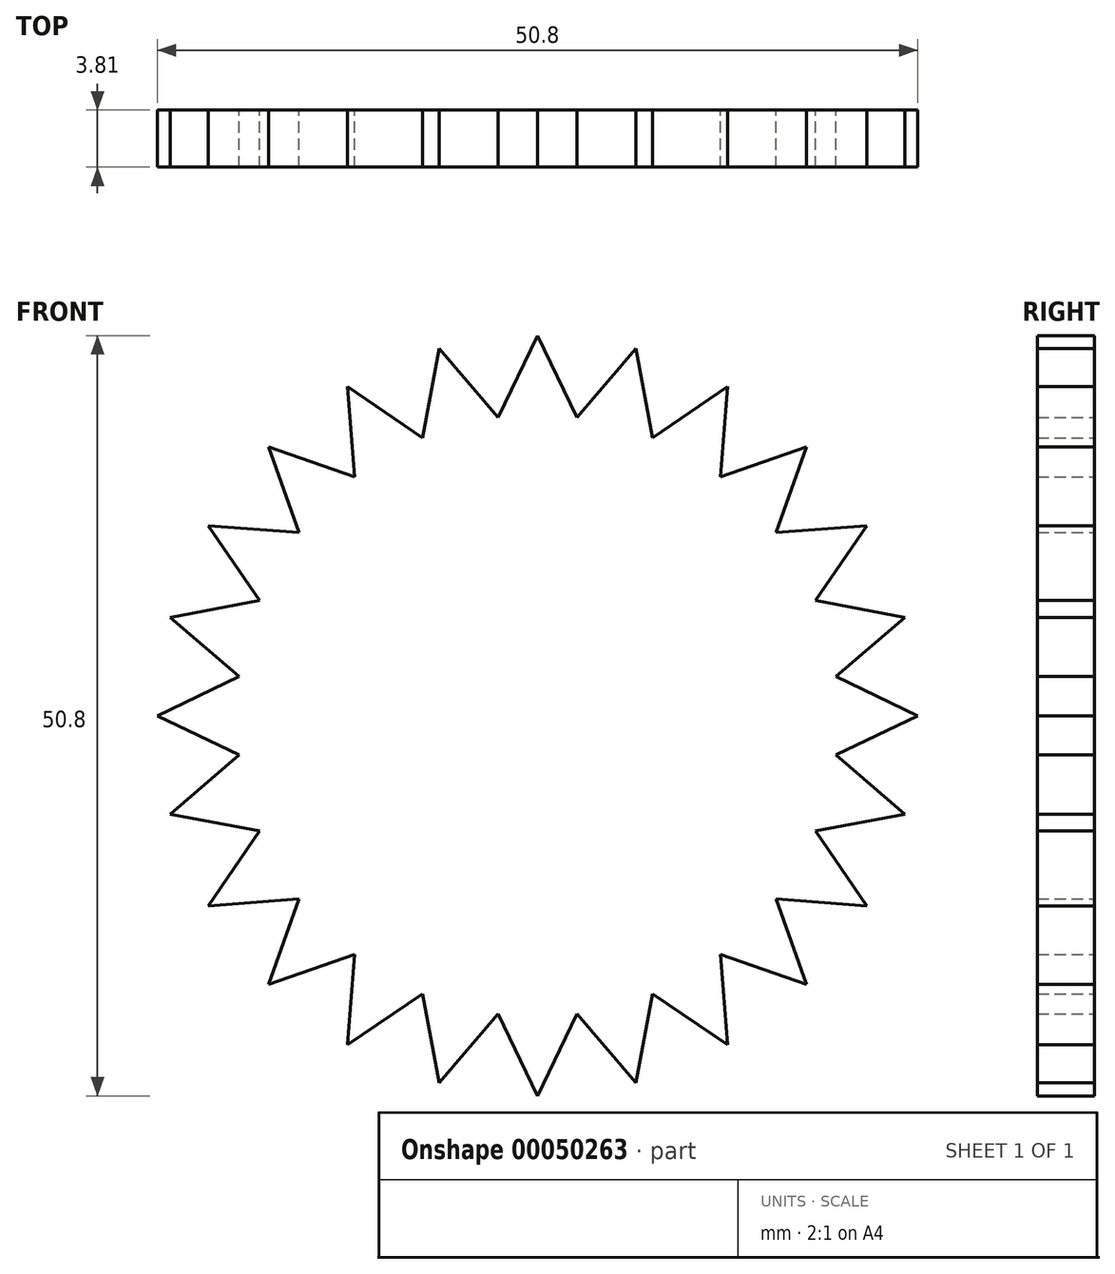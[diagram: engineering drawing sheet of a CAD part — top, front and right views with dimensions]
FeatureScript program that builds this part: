
annotation { "Feature Type Name" : "Feature", "Feature Type Description" : "" }
export const myFeature = defineFeature(function(context is Context, id is Id, definition is map)
    precondition{}
    {
        {
            var Q0;
            Q0=qCreatedBy(makeId("Front.planeOp"),FACE);
            var sketch = newSketch(context, id + "F0", { "sketchPlane" : qUnion([Q0])});
            skLineSegment(sketch, "E0", {"start": v(0, 0) * mm, "end": v(25.4, 0) * mm});
            skLineSegment(sketch, "E1", {"start": v(0, 0) * mm, "end": v(0, 25.4) * mm});
            skLineSegment(sketch, "E2", {"start": v(0, 0) * mm, "end": v(-25.4, 0) * mm});
            skLineSegment(sketch, "E3", {"start": v(0, 0) * mm, "end": v(0, -25.4) * mm});
            skLineSegment(sketch, "E4", {"start": v(0, 0) * mm, "end": v(24.53, -6.57) * mm});
            skLineSegment(sketch, "E5", {"start": v(0, 0) * mm, "end": v(24.53, 6.57) * mm});
            skLineSegment(sketch, "E6", {"start": v(0, 0) * mm, "end": v(22, 12.7) * mm});
            skLineSegment(sketch, "E7", {"start": v(0, 0) * mm, "end": v(17.96, 17.96) * mm});
            skLineSegment(sketch, "E8", {"start": v(0, 0) * mm, "end": v(12.7, 22) * mm});
            skLineSegment(sketch, "E9", {"start": v(0, 0) * mm, "end": v(6.57, 24.53) * mm});
            skLineSegment(sketch, "E10", {"start": v(0, 0) * mm, "end": v(-6.57, -24.53) * mm});
            skLineSegment(sketch, "E11", {"start": v(0, 0) * mm, "end": v(22, -12.7) * mm});
            skLineSegment(sketch, "E12", {"start": v(0, 0) * mm, "end": v(17.96, -17.96) * mm});
            skLineSegment(sketch, "E13", {"start": v(0, 0) * mm, "end": v(12.7, -22) * mm});
            skLineSegment(sketch, "E14", {"start": v(0, 0) * mm, "end": v(6.57, -24.53) * mm});
            skLineSegment(sketch, "E15", {"start": v(0, 0) * mm, "end": v(-12.7, -22) * mm});
            skLineSegment(sketch, "E16", {"start": v(0, 0) * mm, "end": v(-17.96, -17.96) * mm});
            skLineSegment(sketch, "E17", {"start": v(0, 0) * mm, "end": v(-22, -12.7) * mm});
            skLineSegment(sketch, "E18", {"start": v(0, 0) * mm, "end": v(-24.53, -6.57) * mm});
            skLineSegment(sketch, "E19", {"start": v(0, 0) * mm, "end": v(-24.53, 6.57) * mm});
            skLineSegment(sketch, "E20", {"start": v(0, 0) * mm, "end": v(-22, 12.7) * mm});
            skLineSegment(sketch, "E21", {"start": v(0, 0) * mm, "end": v(-17.96, 17.96) * mm});
            skLineSegment(sketch, "E22", {"start": v(0, 0) * mm, "end": v(-12.7, 22) * mm});
            skLineSegment(sketch, "E23", {"start": v(0, 0) * mm, "end": v(-6.57, 24.53) * mm});
            skPoint(sketch, "E24.startSnap0", {"position": v(23.27, 9.64) * mm});
            skLineSegment(sketch, "E25", {"start": v(3.29, 24.97) * mm, "end": v(2.62, 19.93) * mm});
            skLineSegment(sketch, "E26", {"start": v(19.98, 15.33) * mm, "end": v(15.95, 12.24) * mm});
            skLineSegment(sketch, "E27", {"start": v(23.27, 9.64) * mm, "end": v(18.57, 7.7) * mm});
            skLineSegment(sketch, "E28", {"start": v(24.97, 3.29) * mm, "end": v(19.93, 2.62) * mm});
            skLineSegment(sketch, "E29", {"start": v(24.97, -3.29) * mm, "end": v(19.93, -2.62) * mm});
            skLineSegment(sketch, "E30", {"start": v(23.27, -9.64) * mm, "end": v(18.57, -7.7) * mm});
            skLineSegment(sketch, "E31", {"start": v(19.98, -15.33) * mm, "end": v(15.95, -12.24) * mm});
            skLineSegment(sketch, "E32", {"start": v(15.33, -19.98) * mm, "end": v(12.24, -15.95) * mm});
            skLineSegment(sketch, "E33", {"start": v(9.64, -23.27) * mm, "end": v(7.7, -18.57) * mm});
            skLineSegment(sketch, "E34", {"start": v(3.29, -24.97) * mm, "end": v(2.62, -19.93) * mm});
            skLineSegment(sketch, "E35", {"start": v(-3.29, -24.97) * mm, "end": v(-2.62, -19.93) * mm});
            skLineSegment(sketch, "E36", {"start": v(-9.64, -23.27) * mm, "end": v(-7.7, -18.57) * mm});
            skLineSegment(sketch, "E37", {"start": v(-15.33, -19.98) * mm, "end": v(-12.24, -15.95) * mm});
            skLineSegment(sketch, "E38", {"start": v(-19.98, -15.33) * mm, "end": v(-15.95, -12.24) * mm});
            skLineSegment(sketch, "E39", {"start": v(-23.27, -9.64) * mm, "end": v(-18.57, -7.7) * mm});
            skLineSegment(sketch, "E40", {"start": v(-24.97, -3.29) * mm, "end": v(-19.93, -2.62) * mm});
            skLineSegment(sketch, "E41", {"start": v(-24.97, 3.29) * mm, "end": v(-19.93, 2.62) * mm});
            skLineSegment(sketch, "E42", {"start": v(-23.27, 9.64) * mm, "end": v(-18.57, 7.7) * mm});
            skLineSegment(sketch, "E43", {"start": v(-19.98, 15.33) * mm, "end": v(-15.95, 12.24) * mm});
            skLineSegment(sketch, "E44", {"start": v(-15.33, 19.98) * mm, "end": v(-12.24, 15.95) * mm});
            skLineSegment(sketch, "E45", {"start": v(-9.64, 23.27) * mm, "end": v(-7.7, 18.57) * mm});
            skLineSegment(sketch, "E46", {"start": v(-3.29, 24.97) * mm, "end": v(-2.62, 19.93) * mm});
            skLineSegment(sketch, "E47", {"start": v(0, 25.4) * mm, "end": v(2.62, 19.93) * mm});
            skLineSegment(sketch, "E48", {"start": v(2.62, 19.93) * mm, "end": v(6.57, 24.53) * mm});
            skLineSegment(sketch, "E49", {"start": v(6.57, 24.53) * mm, "end": v(7.7, 18.57) * mm});
            skLineSegment(sketch, "E50", {"start": v(7.7, 18.57) * mm, "end": v(12.7, 22) * mm});
            skLineSegment(sketch, "E51", {"start": v(12.7, 22) * mm, "end": v(12.24, 15.95) * mm});
            skLineSegment(sketch, "E52", {"start": v(12.24, 15.95) * mm, "end": v(17.96, 17.96) * mm});
            skLineSegment(sketch, "E53", {"start": v(17.96, 17.96) * mm, "end": v(15.95, 12.24) * mm});
            skLineSegment(sketch, "E54", {"start": v(15.95, 12.24) * mm, "end": v(22, 12.7) * mm});
            skLineSegment(sketch, "E55", {"start": v(22, 12.7) * mm, "end": v(18.57, 7.7) * mm});
            skLineSegment(sketch, "E56", {"start": v(24.53, 6.57) * mm, "end": v(18.57, 7.7) * mm});
            skLineSegment(sketch, "E57", {"start": v(24.53, 6.57) * mm, "end": v(19.93, 2.62) * mm});
            skLineSegment(sketch, "E58", {"start": v(19.93, 2.62) * mm, "end": v(25.4, 0) * mm});
            skLineSegment(sketch, "E59", {"start": v(25.4, 0) * mm, "end": v(19.93, -2.62) * mm});
            skLineSegment(sketch, "E60", {"start": v(19.93, -2.62) * mm, "end": v(24.53, -6.57) * mm});
            skLineSegment(sketch, "E61", {"start": v(22, -12.7) * mm, "end": v(18.57, -7.7) * mm});
            skLineSegment(sketch, "E62", {"start": v(24.53, -6.57) * mm, "end": v(18.57, -7.7) * mm});
            skLineSegment(sketch, "E63", {"start": v(22, -12.7) * mm, "end": v(15.95, -12.24) * mm});
            skLineSegment(sketch, "E64", {"start": v(15.95, -12.24) * mm, "end": v(17.96, -17.96) * mm});
            skLineSegment(sketch, "E65", {"start": v(17.96, -17.96) * mm, "end": v(12.24, -15.95) * mm});
            skLineSegment(sketch, "E66", {"start": v(12.7, -22) * mm, "end": v(12.24, -15.95) * mm});
            skLineSegment(sketch, "E67", {"start": v(6.57, -24.53) * mm, "end": v(7.7, -18.57) * mm});
            skLineSegment(sketch, "E68", {"start": v(7.7, -18.57) * mm, "end": v(12.7, -22) * mm});
            skLineSegment(sketch, "E69", {"start": v(0, -25.4) * mm, "end": v(2.62, -19.93) * mm});
            skLineSegment(sketch, "E70", {"start": v(6.57, -24.53) * mm, "end": v(2.62, -19.93) * mm});
            skLineSegment(sketch, "E71", {"start": v(0, -25.4) * mm, "end": v(-2.62, -19.93) * mm});
            skLineSegment(sketch, "E72", {"start": v(-6.57, -24.53) * mm, "end": v(-2.62, -19.93) * mm});
            skLineSegment(sketch, "E73", {"start": v(-6.57, -24.53) * mm, "end": v(-7.7, -18.57) * mm});
            skLineSegment(sketch, "E74", {"start": v(-7.7, -18.57) * mm, "end": v(-12.7, -22) * mm});
            skLineSegment(sketch, "E75", {"start": v(-12.7, -22) * mm, "end": v(-12.24, -15.95) * mm});
            skLineSegment(sketch, "E76", {"start": v(-12.24, -15.95) * mm, "end": v(-17.96, -17.96) * mm});
            skLineSegment(sketch, "E77", {"start": v(-17.96, -17.96) * mm, "end": v(-15.95, -12.24) * mm});
            skLineSegment(sketch, "E78", {"start": v(-22, -12.7) * mm, "end": v(-15.95, -12.24) * mm});
            skLineSegment(sketch, "E79", {"start": v(-22, -12.7) * mm, "end": v(-18.57, -7.7) * mm});
            skLineSegment(sketch, "E80", {"start": v(-18.57, -7.7) * mm, "end": v(-24.53, -6.57) * mm});
            skLineSegment(sketch, "E81", {"start": v(-24.53, -6.57) * mm, "end": v(-19.93, -2.62) * mm});
            skLineSegment(sketch, "E82", {"start": v(-19.93, -2.62) * mm, "end": v(-25.4, 0) * mm});
            skLineSegment(sketch, "E83", {"start": v(-25.4, 0) * mm, "end": v(-19.93, 2.62) * mm});
            skLineSegment(sketch, "E84", {"start": v(-19.93, 2.62) * mm, "end": v(-24.53, 6.57) * mm});
            skLineSegment(sketch, "E85", {"start": v(-24.53, 6.57) * mm, "end": v(-18.57, 7.7) * mm});
            skLineSegment(sketch, "E86", {"start": v(-18.57, 7.7) * mm, "end": v(-22, 12.7) * mm});
            skLineSegment(sketch, "E87", {"start": v(-22, 12.7) * mm, "end": v(-15.95, 12.24) * mm});
            skLineSegment(sketch, "E88", {"start": v(-15.95, 12.24) * mm, "end": v(-17.96, 17.96) * mm});
            skLineSegment(sketch, "E89", {"start": v(-17.96, 17.96) * mm, "end": v(-12.24, 15.95) * mm});
            skLineSegment(sketch, "E90", {"start": v(-12.24, 15.95) * mm, "end": v(-12.7, 22) * mm});
            skLineSegment(sketch, "E91", {"start": v(-12.7, 22) * mm, "end": v(-7.7, 18.57) * mm});
            skLineSegment(sketch, "E92", {"start": v(-7.7, 18.57) * mm, "end": v(-6.57, 24.53) * mm});
            skLineSegment(sketch, "E93", {"start": v(-6.57, 24.53) * mm, "end": v(-2.62, 19.93) * mm});
            skLineSegment(sketch, "E94", {"start": v(-2.62, 19.93) * mm, "end": v(0, 25.4) * mm});
            skSolve(sketch);
        }
        {
            var Q0;
            Q0=qSketchRegion(id+"F0",true);
            extrude(context, id + "F1", {"entities" : qUnion([Q0]), "depth" : 3.8 * mm});
        }
    });
